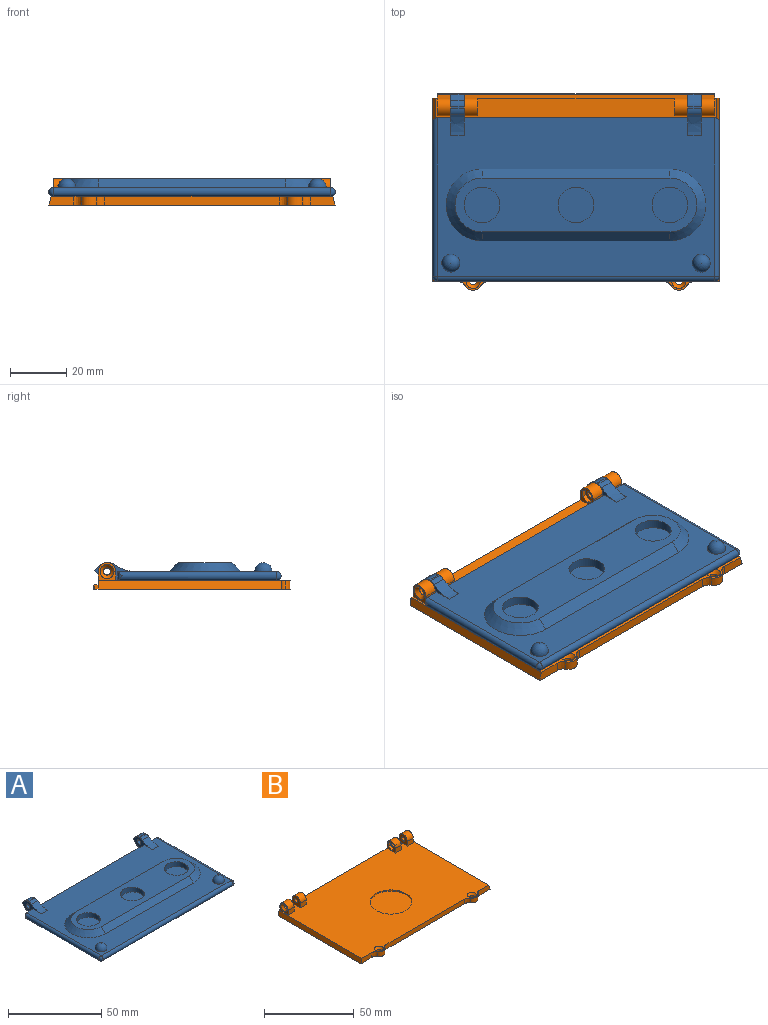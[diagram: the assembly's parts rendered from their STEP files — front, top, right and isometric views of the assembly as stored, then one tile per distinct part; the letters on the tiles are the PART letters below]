
ASSEMBLY  parts=2 mates=1
PART A: 45 faces, bbox 102.7x67.3x7.5 mm
  f0: cylinder r=3.17mm len=4.78mm, axis (-1,0,0), area 13.2mm2, adj f6,f20,f21,f33
  f1: cylinder r=3.17mm len=4.78mm, axis (-1,0,0), area 11.4mm2, adj f23,f24,f25,f30
  f2: plane 4.76x3.18mm, normal (0,1,0), area 15.1mm2, adj f4,f6,f24,f41
  f3: plane 79.35x3.18mm, normal (0,1,0), area 251.9mm2, adj f4,f6,f21,f23
  f4: plane 98.43x56.36mm, normal (0,0,1), area 3222.5mm2, adj f2,f3,f5,f14,f15,f16,f17,f18
  f5: plane 4.76x3.18mm, normal (0,1,0), area 15.1mm2, adj f4,f6,f20,f38
  f6: plane 98.43x60.18mm, normal (0,0,-1), area 5583.3mm2, adj f0,f2,f3,f5,f20,f21,f23,f24
  f7: cylinder r=6.35mm len=12.7mm, axis (0,0,-1), area 126.7mm2, adj f10,f11
  f8: cylinder r=6.35mm len=12.7mm, axis (0,0,-1), area 126.7mm2, adj f10,f12
  f9: cylinder r=6.35mm len=12.7mm, axis (0,0,-1), area 126.7mm2, adj f10,f13
  f10: plane 85.73x19.05mm, normal (0,0,1), area 1175.2mm2, adj f7,f8,f9,f14,f15,f16,f17
  f11: plane 12.7x12.7mm, normal (0,0,1), area 126.7mm2, adj f7
  f12: plane 12.7x12.7mm, normal (0,0,1), area 126.7mm2, adj f8
  f13: plane 12.7x12.7mm, normal (0,0,1), area 126.7mm2, adj f9
  f14: plane 66.68x3.18mm, normal (0,-0.71,0.71), area 299.4mm2, adj f4,f10,f15,f16
  f15: cone r=9.53mm half-angle=45deg, axis (0,0,-1), area 156.8mm2, adj f4,f10,f14,f17
  f16: cone r=9.53mm half-angle=45deg, axis (0,0,-1), area 156.8mm2, adj f4,f10,f14,f17
  f17: plane 66.68x3.18mm, normal (0,0.71,0.71), area 299.4mm2, adj f4,f10,f15,f16
  f18: sphere r=3.17mm, area 63.3mm2, adj f4
  f19: sphere r=3.17mm, area 63.3mm2, adj f4
  f20: plane 15.72x7.45mm, normal (1,0,0), area 38.8mm2, adj f0,f4,f5,f6,f22,f28,f29,f32
  f21: plane 15.72x7.45mm, normal (-1,0,0), area 38.8mm2, adj f0,f3,f4,f6,f22,f28,f29,f32
  f22: plane 4.78x0.65mm, normal (0,0,1), area 3.1mm2, adj f20,f21,f28,f29
  f23: plane 15.75x7.45mm, normal (1,0,0), area 38.9mm2, adj f1,f3,f4,f6,f25,f26,f27,f30
  f24: plane 15.75x7.45mm, normal (-1,0,0), area 38.9mm2, adj f1,f2,f4,f6,f25,f26,f27,f30
  f25: plane 4.78x0.65mm, normal (0,0,1), area 3.1mm2, adj f1,f23,f24,f27
  f26: cylinder r=3.17mm len=4.78mm, axis (-1,0,0), area 13.2mm2, adj f6,f23,f24,f31
  f27: cylinder r=3.17mm len=4.78mm, axis (1,0,0), area 9.8mm2, adj f23,f24,f25,f34
  f28: cylinder r=3.17mm len=4.78mm, axis (-1,0,0), area 13.1mm2, adj f20,f21,f22,f32
  f29: cylinder r=3.17mm len=4.78mm, axis (1,0,0), area 9.8mm2, adj f20,f21,f22,f35
  f30: plane 4.78x2.3mm, normal (0,0.64,0.77), area 14.3mm2, adj f1,f23,f24,f31
  f31: plane 4.78x2.43mm, normal (0,0.77,-0.64), area 15.1mm2, adj f23,f24,f26,f30
  f32: plane 4.78x2.03mm, normal (0,0.64,0.77), area 12.7mm2, adj f20,f21,f28,f33
  f33: plane 4.78x2.4mm, normal (0,0.77,-0.64), area 15mm2, adj f0,f20,f21,f32
  f34: bspline ~7.62x5.25mm, area 39.1mm2, adj f4,f23,f24,f27
  f35: bspline ~7.62x5.25mm, area 39.1mm2, adj f4,f20,f21,f29
  f36: cylinder r=1.27mm len=4.78mm, axis (-1,0,0), area 38.1mm2, adj f23,f24
  f37: cylinder r=1.27mm len=4.78mm, axis (1,0,0), area 38.1mm2, adj f20,f21
  f38: cylinder r=1.59mm len=3.18mm, axis (0,0,1), area 4mm2, adj f5,f39
  f39: cylinder r=1.59mm len=56.36mm, axis (0,-1,0), area 277.1mm2, adj f4,f6,f38,f40
  f40: sphere r=1.59mm, area 7.9mm2, adj f39,f42
  f41: cylinder r=1.59mm len=3.18mm, axis (0,0,-1), area 4mm2, adj f2,f43
  f42: cylinder r=1.59mm len=98.43mm, axis (-1,0,0), area 490.9mm2, adj f4,f6,f40,f44
  f43: cylinder r=1.59mm len=56.36mm, axis (0,1,0), area 277.1mm2, adj f4,f6,f41,f44
  f44: sphere r=1.59mm, area 7.9mm2, adj f42,f43
PART B: 66 faces, bbox 101.9x70.2x10.1 mm
  f0: plane 6.35x6.35mm, normal (-1,0,0), area 16.2mm2, adj f2,f9,f37,f39,f49,f50,f51,f52
  f1: plane 6.35x6.35mm, normal (1,0,0), area 16.2mm2, adj f2,f9,f32,f40,f42,f43,f44,f45
  f2: plane 100.27x68.62mm, normal (0,0,1), area 5950.8mm2, adj f0,f1,f3,f4,f8,f9,f12,f13
  f3: plane 8.77x3.18mm, normal (0,-1,0), area 26.6mm2, adj f2,f7,f15,f27,f65
  f4: plane 62x3.18mm, normal (0,-1,0), area 196.9mm2, adj f2,f7,f14,f16
  f5: plane 97.94x1.09mm, normal (0,1,0), area 107mm2, adj f22,f23,f24,f25
  f6: plane 98.45x1.32mm, normal (0,0,1), area 130mm2, adj f9,f10,f11,f24
  f7: plane 101.46x69.94mm, normal (0,0,-1), area 6733.1mm2, adj f3,f4,f8,f9,f10,f11,f12,f13
  f8: plane 8.77x3.18mm, normal (0,-1,0), area 26.6mm2, adj f2,f7,f17,f26,f64
  f9: plane 101.53x6.35mm, normal (0,1,0), area 222.8mm2, adj f0,f1,f2,f6,f7,f10,f11,f26
  f10: plane 1.6x1.32mm, normal (1,0,0), area 2.1mm2, adj f6,f7,f9,f25
  f11: plane 1.6x1.32mm, normal (-1,0,0), area 2.1mm2, adj f6,f7,f9,f22
  f12: cylinder r=3.17mm len=5.5mm, axis (0,0,1), area 21.1mm2, adj f2,f7,f14,f15
  f13: cylinder r=3.17mm len=5.5mm, axis (0,0,-1), area 21.1mm2, adj f2,f7,f16,f17
  f14: bspline ~3.49x2.75mm, area 10.6mm2, adj f2,f4,f7,f12
  f15: bspline ~3.49x2.75mm, area 10.6mm2, adj f2,f3,f7,f12
  f16: bspline ~3.49x2.75mm, area 10.6mm2, adj f2,f4,f7,f13
  f17: bspline ~3.49x2.75mm, area 10.6mm2, adj f2,f7,f8,f13
  f18: cylinder r=1.27mm len=2.54mm, axis (0,0,1), area 14.2mm2, adj f7,f20
  f19: cylinder r=1.27mm len=2.54mm, axis (0,0,1), area 14.2mm2, adj f7,f21
  f20: cone r=1.27mm half-angle=41deg, axis (0,0,1), area 21.8mm2, adj f2,f18
  f21: cone r=1.27mm half-angle=41deg, axis (0,0,1), area 21.8mm2, adj f2,f19
  f22: cylinder r=0.25mm len=1.6mm, axis (0,0,-1), area 0.5mm2, adj f5,f11,f23,f24
  f23: cylinder r=0.25mm len=98.45mm, axis (1,0,0), area 39.2mm2, adj f5,f7,f22,f25
  f24: cylinder r=0.25mm len=98.45mm, axis (-1,0,0), area 39.2mm2, adj f5,f6,f22,f25
  f25: cylinder r=0.25mm len=1.6mm, axis (0,0,1), area 0.5mm2, adj f5,f10,f23,f24
  f26: cylinder r=0.25mm len=65.08mm, axis (0,1,0), area 17.3mm2, adj f7,f8,f9,f64
  f27: cylinder r=0.25mm len=65.08mm, axis (0,-1,0), area 17.3mm2, adj f3,f7,f9,f65
  f28: plane 6.35x6.35mm, normal (-1,0,0), area 16.6mm2, adj f2,f9,f29,f41,f61
  f29: plane 4.76x3.18mm, normal (0,-1,0), area 15.1mm2, adj f2,f28,f30,f41
  f30: plane 6.35x6.35mm, normal (1,0,0), area 30.9mm2, adj f2,f9,f29,f41,f59
  f31: plane 6.35x6.35mm, normal (-1,0,0), area 30.9mm2, adj f2,f9,f32,f40,f57
  f32: plane 4.76x3.18mm, normal (0,-1,0), area 15.1mm2, adj f1,f2,f31,f40
  f33: plane 6.35x6.35mm, normal (1,0,0), area 16.6mm2, adj f2,f9,f35,f38,f60
  f34: plane 6.35x6.35mm, normal (-1,0,0), area 30.9mm2, adj f2,f9,f35,f38,f58
  f35: plane 4.76x3.18mm, normal (0,-1,0), area 15.1mm2, adj f2,f33,f34,f38
  f36: plane 6.35x6.35mm, normal (1,0,0), area 30.9mm2, adj f2,f9,f37,f39,f56
  f37: plane 4.76x3.18mm, normal (0,-1,0), area 15.1mm2, adj f0,f2,f36,f39
  f38: cylinder r=3.17mm len=6.35mm, axis (-1,0,0), area 47.5mm2, adj f9,f33,f34,f35
  f39: cylinder r=3.17mm len=6.35mm, axis (-1,0,0), area 47.5mm2, adj f0,f9,f36,f37
  f40: cylinder r=3.17mm len=6.35mm, axis (-1,0,0), area 47.5mm2, adj f1,f9,f31,f32
  f41: cylinder r=3.17mm len=6.35mm, axis (-1,0,0), area 47.5mm2, adj f9,f28,f29,f30
  f42: plane 2.39x1.6mm, normal (0,0.5,-0.87), area 4.4mm2, adj f1,f43,f47,f48
  f43: plane 2.76x1.6mm, normal (0,1,0), area 4.4mm2, adj f1,f42,f44,f48
  f44: plane 2.39x1.6mm, normal (0,0.5,0.87), area 4.4mm2, adj f1,f43,f45,f48
  f45: plane 2.39x1.6mm, normal (0,-0.5,0.87), area 4.4mm2, adj f1,f44,f46,f48
  f46: plane 2.76x1.6mm, normal (0,-1,0), area 4.4mm2, adj f1,f45,f47,f48
  f47: plane 2.39x1.6mm, normal (0,-0.5,-0.87), area 4.4mm2, adj f1,f42,f46,f48
  f48: plane 5.51x4.78mm, normal (1,0,0), area 14.7mm2, adj f42,f43,f44,f45,f46,f47,f57
  f49: plane 2.39x1.59mm, normal (0,-0.5,-0.87), area 4.4mm2, adj f0,f50,f54,f55
  f50: plane 2.76x1.59mm, normal (0,-1,0), area 4.4mm2, adj f0,f49,f51,f55
  f51: plane 2.39x1.59mm, normal (0,-0.5,0.87), area 4.4mm2, adj f0,f50,f52,f55
  f52: plane 2.39x1.59mm, normal (0,0.5,0.87), area 4.4mm2, adj f0,f51,f53,f55
  f53: plane 2.76x1.59mm, normal (0,1,0), area 4.4mm2, adj f0,f52,f54,f55
  f54: plane 2.39x1.59mm, normal (0,0.5,-0.87), area 4.4mm2, adj f0,f49,f53,f55
  f55: plane 5.51x4.78mm, normal (-1,0,0), area 14.7mm2, adj f49,f50,f51,f52,f53,f54,f56
  f56: cylinder r=1.27mm len=3.18mm, axis (-1,0,0), area 25.3mm2, adj f36,f55
  f57: cylinder r=1.27mm len=3.16mm, axis (1,0,0), area 25.2mm2, adj f31,f48
  f58: cylinder r=1.27mm len=3.37mm, axis (1,0,0), area 26.9mm2, adj f34,f60
  f59: cylinder r=1.27mm len=3.37mm, axis (-1,0,0), area 26.9mm2, adj f30,f61
  f60: cone r=1.27mm half-angle=41deg, axis (1,0,0), area 21.8mm2, adj f33,f58
  f61: cone r=1.27mm half-angle=41deg, axis (-1,0,0), area 21.8mm2, adj f28,f59
  f62: cylinder r=11.63mm len=23.26mm, axis (0,0,1), area 57.9mm2, adj f2,f63
  f63: plane 23.26x23.26mm, normal (0,0,1), area 425mm2, adj f62
  f64: plane 65.08x3.05mm, normal (-0.97,0,0.26), area 205.3mm2, adj f2,f8,f9,f26
  f65: plane 65.08x3.05mm, normal (0.97,0,0.26), area 205.3mm2, adj f2,f3,f9,f27
PLACE A rot(axis=(1,0,0),0deg) t=(0.61,0,-1.71)mm
PLACE B t=(0.61,1.92,-4.89)mm fixed
MATE revolute A.f0 <-> B.f41  axis (-1,0,0) through (-43.84,30.42,1.46)mm
